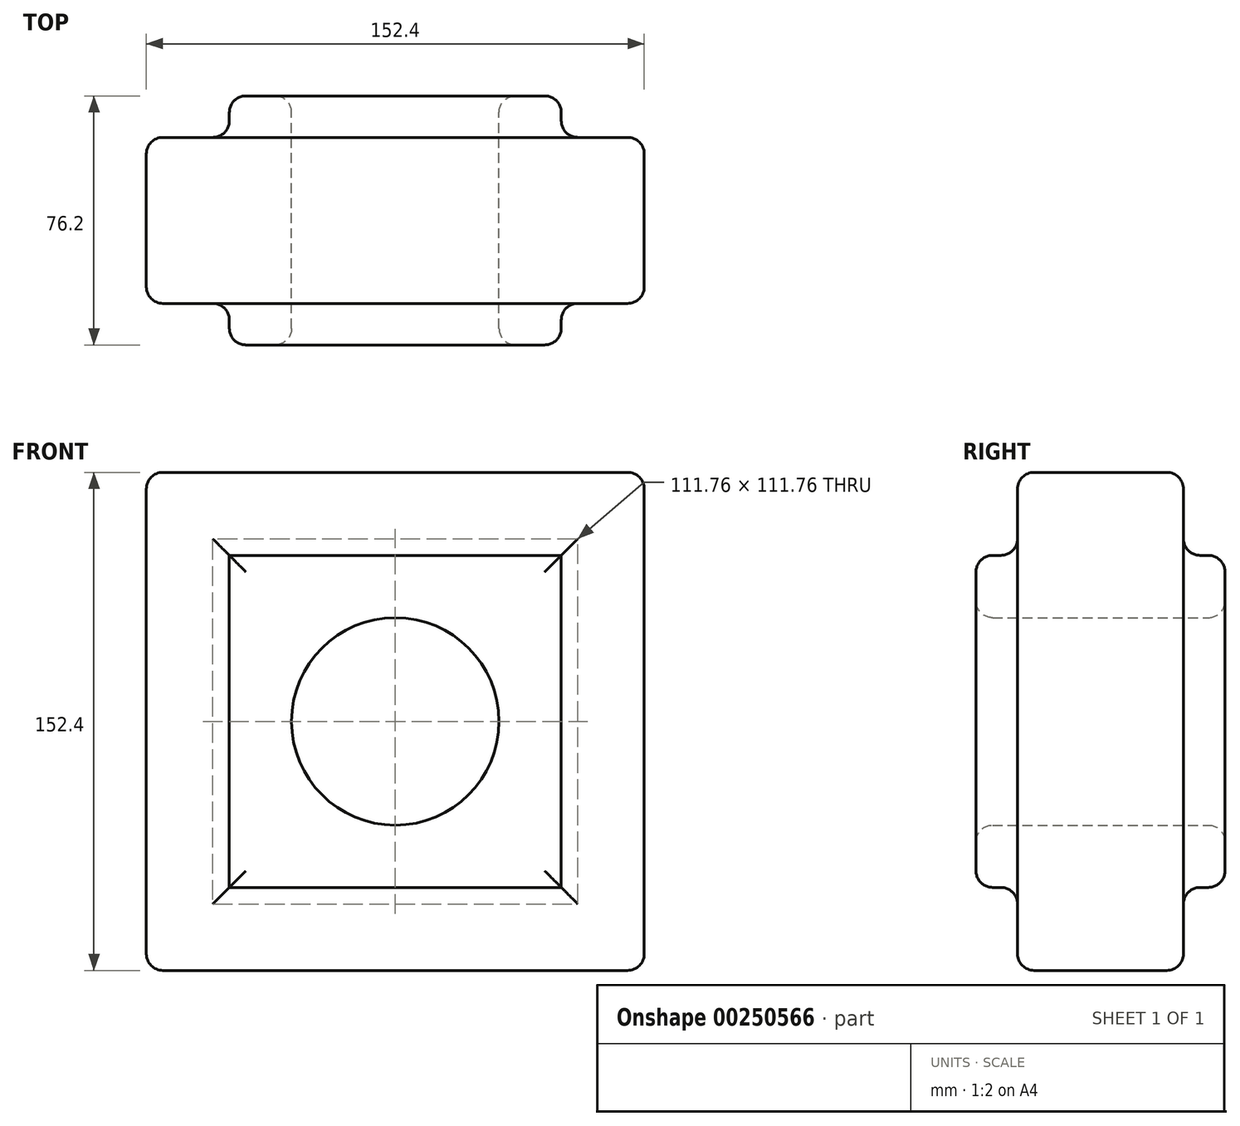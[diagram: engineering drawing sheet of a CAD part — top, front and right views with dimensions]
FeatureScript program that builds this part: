
annotation { "Feature Type Name" : "Feature", "Feature Type Description" : "" }
export const myFeature = defineFeature(function(context is Context, id is Id, definition is map)
    precondition{}
    {
        {
            var Q0;
            Q0=qCreatedBy(makeId("Front.planeOp"),FACE);
            var sketch = newSketch(context, id + "F0", { "sketchPlane" : qUnion([Q0])});
            skCircle(sketch, "E0", {"center": v(0, 0) * mm, "radius": 31.75 * mm});
            skLineSegment(sketch, "E1.bottom", {"start": v(50.8, 50.8) * mm, "end": v(-50.8, 50.8) * mm});
            skLineSegment(sketch, "E1.top", {"start": v(50.8, -50.8) * mm, "end": v(-50.8, -50.8) * mm});
            skLineSegment(sketch, "E1.left", {"start": v(50.8, 50.8) * mm, "end": v(50.8, -50.8) * mm});
            skLineSegment(sketch, "E1.right", {"start": v(-50.8, 50.8) * mm, "end": v(-50.8, -50.8) * mm});
            skLineSegment(sketch, "E2.bottom", {"start": v(76.2, 76.2) * mm, "end": v(-76.2, 76.2) * mm});
            skLineSegment(sketch, "E2.top", {"start": v(76.2, -76.2) * mm, "end": v(-76.2, -76.2) * mm});
            skLineSegment(sketch, "E2.left", {"start": v(76.2, 76.2) * mm, "end": v(76.2, -76.2) * mm});
            skLineSegment(sketch, "E2.right", {"start": v(-76.2, 76.2) * mm, "end": v(-76.2, -76.2) * mm});
            skSolve(sketch);
        }
        {
            var Q0;
            Q0=makeQuery(id+"F0.imprint","IMPRINT",FACE,{"disambiguationData":[TD([[makeQuery(id+"F0.imprint","IMPRINT",EDGE,{"derivedFrom":sQuery(id+"F0.wireOp",EDGE,"E0")}),-1.0]])]});
            extrude(context, id + "F1", {"entities" : qUnion([Q0]), "endBound" : BoundingType.SYMMETRIC, "depth" : 76.2 * mm});
        }
        {
            var Q0;
            Q0=makeQuery(id+"F0.imprint","IMPRINT",FACE,{"disambiguationData":[TD([[makeQuery(id+"F0.imprint","IMPRINT",EDGE,{"derivedFrom":sQuery(id+"F0.wireOp",EDGE,"E1.bottom")}),-1.0]])]});
            extrude(context, id + "F2", {"entities" : qUnion([Q0]), "operationType" : NewBodyOperationType.ADD, "endBound" : BoundingType.SYMMETRIC, "depth" : 50.8 * mm});
        }
        {
            var Q0;
            Q0=makeQuery(id+"F2.opExtrude","CAP_FACE",FACE,{"disambiguationData":[OSD([sQuery(id+"F0.wireOp",EDGE,"E1.bottom"),sQuery(id+"F0.wireOp",EDGE,"E1.top"),sQuery(id+"F0.wireOp",EDGE,"E1.left"),sQuery(id+"F0.wireOp",EDGE,"E1.right"),sQuery(id+"F0.wireOp",EDGE,"E2.bottom"),sQuery(id+"F0.wireOp",EDGE,"E2.top"),sQuery(id+"F0.wireOp",EDGE,"E2.left"),sQuery(id+"F0.wireOp",EDGE,"E2.right")])],"isStart":true});
            var Q1;
            Q1=makeQuery(id+"F1.opExtrude","CAP_FACE",FACE,{"disambiguationData":[OSD([sQuery(id+"F0.wireOp",EDGE,"E0"),sQuery(id+"F0.wireOp",EDGE,"E1.bottom"),sQuery(id+"F0.wireOp",EDGE,"E1.top"),sQuery(id+"F0.wireOp",EDGE,"E1.left"),sQuery(id+"F0.wireOp",EDGE,"E1.right")])],"isStart":true});
            var Q2;
            Q2=makeQuery(id+"F1.opExtrude","CAP_FACE",FACE,{"disambiguationData":[OSD([sQuery(id+"F0.wireOp",EDGE,"E0"),sQuery(id+"F0.wireOp",EDGE,"E1.bottom"),sQuery(id+"F0.wireOp",EDGE,"E1.top"),sQuery(id+"F0.wireOp",EDGE,"E1.left"),sQuery(id+"F0.wireOp",EDGE,"E1.right")])],"isStart":false});
            var Q3;
            Q3=makeQuery(id+"F2.opExtrude","CAP_FACE",FACE,{"disambiguationData":[OSD([sQuery(id+"F0.wireOp",EDGE,"E1.bottom"),sQuery(id+"F0.wireOp",EDGE,"E1.top"),sQuery(id+"F0.wireOp",EDGE,"E1.left"),sQuery(id+"F0.wireOp",EDGE,"E1.right"),sQuery(id+"F0.wireOp",EDGE,"E2.bottom"),sQuery(id+"F0.wireOp",EDGE,"E2.top"),sQuery(id+"F0.wireOp",EDGE,"E2.left"),sQuery(id+"F0.wireOp",EDGE,"E2.right")])],"isStart":false});
            var Q4;
            Q4=makeQuery(id+"F2.opExtrude","SWEPT_FACE",FACE,{"disambiguationData":[OSD([sQuery(id+"F0.wireOp",EDGE,"E2.top")])]});
            var Q5;
            Q5=makeQuery(id+"F2.opExtrude","SWEPT_FACE",FACE,{"disambiguationData":[OSD([sQuery(id+"F0.wireOp",EDGE,"E2.left")])]});
            var Q6;
            Q6=makeQuery(id+"F2.opExtrude","SWEPT_FACE",FACE,{"disambiguationData":[OSD([sQuery(id+"F0.wireOp",EDGE,"E2.right")])]});
            fillet(context, id + "F3", {"entities" : qUnion([Q0, Q1, Q2, Q3, Q4, Q5, Q6]), "radius" : 5.08 * mm, "tangentPropagation" : true, "allowEdgeOverflow" : false});
        }
    });
